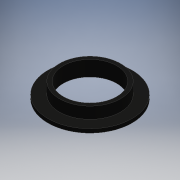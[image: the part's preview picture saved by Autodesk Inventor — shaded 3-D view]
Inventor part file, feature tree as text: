
AUTODESK INVENTOR PART (.ipt)
format: ipt  version: 2016 (Build 200138000, 138)  size: 104,960 bytes
history: native  units: mm
features: extrude x2, other x1, sketch x1
ambient origin geometry x8: Origin, YZ Plane, XZ Plane, XY Plane, X Axis, Y Axis, Z Axis, Center Point
bodies: Body1 (feature_tree)
feature tree (4):
  other  "ソリッド1"
  sketch  "スケッチ1"
  extrude  "押し出し1"  Depth=14.0mm
  extrude  "押し出し2"  Depth=16.0mm
